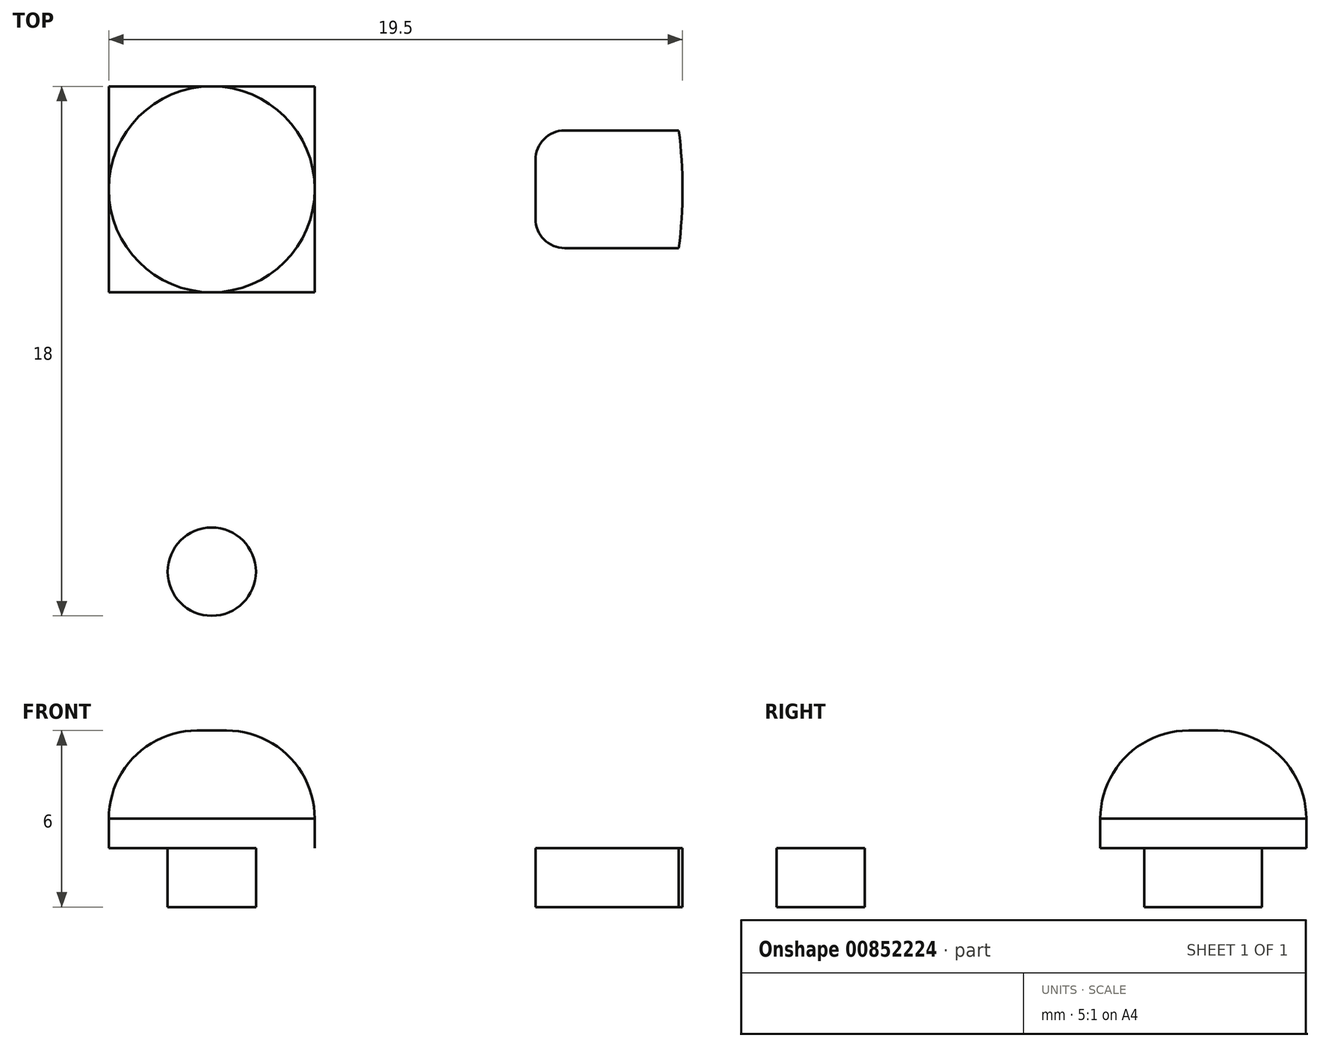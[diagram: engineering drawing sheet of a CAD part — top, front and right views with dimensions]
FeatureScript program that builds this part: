
annotation { "Feature Type Name" : "Feature", "Feature Type Description" : "" }
export const myFeature = defineFeature(function(context is Context, id is Id, definition is map)
    precondition{}
    {
        {
            var Q0;
            Q0=qCreatedBy(makeId("Top.planeOp"),FACE);
            var sketch = newSketch(context, id + "F0", { "sketchPlane" : qUnion([Q0])});
            skCircle(sketch, "E0", {"center": v(0, 0) * mm, "radius": 16 * mm});
            skSolve(sketch);
        }
        {
            var Q0;
            Q0=makeQuery(id+"F0.imprint","IMPRINT",FACE,{"disambiguationData":[TD([[makeQuery(id+"F0.imprint","IMPRINT",EDGE,{"derivedFrom":sQuery(id+"F0.wireOp",EDGE,"E0")}),1.0]])]});
            extrude(context, id + "F1", {"entities" : qUnion([Q0]), "depth" : 2 * mm, "offsetDistance" : 25 * mm});
        }
        {
            var Q0;
            Q0=makeQuery(id+"F1.opExtrude","CAP_FACE",FACE,{"disambiguationData":[OSD([sQuery(id+"F0.wireOp",EDGE,"E0")])],"isStart":false});
            var sketch = newSketch(context, id + "F2", { "sketchPlane" : qUnion([Q0])});
            skLineSegment(sketch, "E1", {"start": v(20.93, 0) * mm, "end": v(-31.8, 0) * mm, "construction": true});
            skLineSegment(sketch, "E2.bottom", {"start": v(-12, 2) * mm, "end": v(-21, 2) * mm});
            skLineSegment(sketch, "E2.top", {"start": v(-12, -2) * mm, "end": v(-21, -2) * mm});
            skLineSegment(sketch, "E2.left", {"start": v(-11, 1) * mm, "end": v(-11, -1) * mm});
            skLineSegment(sketch, "E2.right", {"start": v(-21, 2) * mm, "end": v(-21, -2) * mm});
            skPoint(sketch, "E2.middle", {"position": v(-16, 0) * mm});
            skPoint(sketch, "E3.visualSharp", {"position": v(-11, 2) * mm});
            skArc(sketch, "E3.filletArc", {"start": v(-11, 1) * mm, "mid": v(-11.3, 1.7) * mm, "end": v(-12, 2) * mm});
            skPoint(sketch, "E4.visualSharp", {"position": v(-11, -2) * mm});
            skArc(sketch, "E4.filletArc", {"start": v(-12, -2) * mm, "mid": v(-11.3, -1.7) * mm, "end": v(-11, -1) * mm});
            skLineSegment(sketch, "E5", {"start": v(0, 25.34) * mm, "end": v(0, -23.5) * mm, "construction": true});
            skLineSegment(sketch, "E6.MirrorCS", {"start": v(12, 2) * mm, "end": v(21, 2) * mm});
            skLineSegment(sketch, "E7.MirrorCS", {"start": v(12, -2) * mm, "end": v(21, -2) * mm});
            skPoint(sketch, "E8.MirrorP", {"position": v(11, 2) * mm});
            skPoint(sketch, "E9.MirrorP", {"position": v(11, -2) * mm});
            skLineSegment(sketch, "E10.MirrorCS", {"start": v(21, 2) * mm, "end": v(21, -2) * mm});
            skArc(sketch, "E11.MirrorCS", {"start": v(11, 1) * mm, "mid": v(11.3, 1.7) * mm, "end": v(12, 2) * mm});
            skLineSegment(sketch, "E12.MirrorCS", {"start": v(11, 1) * mm, "end": v(11, -1) * mm});
            skArc(sketch, "E13.MirrorCS", {"start": v(12, -2) * mm, "mid": v(11.3, -1.7) * mm, "end": v(11, -1) * mm});
            skCircle(sketch, "E14", {"center": v(0, 13) * mm, "radius": 1.5 * mm});
            skCircle(sketch, "E15.MirrorC", {"center": v(0, -13) * mm, "radius": 1.5 * mm});
            skSolve(sketch);
        }
        {
            var Q0;
            Q0=makeQuery(id+"F2.imprint","IMPRINT",FACE,{"disambiguationData":[TD([[makeQuery(id+"F2.imprint","IMPRINT",EDGE,{"derivedFrom":sQuery(id+"F2.wireOp",EDGE,"E2.left")}),-1.0]])]});
            var Q1;
            {var subQ0=sQuery(id+"F2.wireOp",EDGE,"E2.right");Q1=makeQuery(id+"F2.imprint","IMPRINT",FACE,{"disambiguationData":[TD([[makeQuery(id+"F2.imprint","IMPRINT",EDGE,{"derivedFrom":subQ0}),1.0]])]});}
            var Q2;
            {var subQ4=sQuery(id+"F2.wireOp",EDGE,"E11.MirrorCS");Q2=makeQuery(id+"F2.imprint","IMPRINT",FACE,{"disambiguationData":[TD([[makeQuery(id+"F2.imprint","IMPRINT",EDGE,{"derivedFrom":subQ4}),-1.0]])]});}
            var Q3;
            {var subQ0=sQuery(id+"F2.wireOp",EDGE,"E10.MirrorCS");Q3=makeQuery(id+"F2.imprint","IMPRINT",FACE,{"disambiguationData":[TD([[makeQuery(id+"F2.imprint","IMPRINT",EDGE,{"derivedFrom":subQ0}),-1.0]])]});}
            var Q4;
            Q4=makeQuery(id+"F2.imprint","IMPRINT",FACE,{"disambiguationData":[TD([[makeQuery(id+"F2.imprint","IMPRINT",EDGE,{"derivedFrom":sQuery(id+"F2.wireOp",EDGE,"E14")}),1.0]])]});
            var Q5;
            Q5=makeQuery(id+"F2.imprint","IMPRINT",FACE,{"disambiguationData":[TD([[makeQuery(id+"F2.imprint","IMPRINT",EDGE,{"derivedFrom":sQuery(id+"F2.wireOp",EDGE,"E15.MirrorC")}),-1.0]])]});
            extrude(context, id + "F3", {"entities" : qUnion([Q0, Q1, Q2, Q3, Q4, Q5]), "operationType" : NewBodyOperationType.REMOVE, "endBound" : BoundingType.THROUGH_ALL, "oppositeDirection" : true, "depth" : 25 * mm, "offsetDistance" : 25 * mm});
        }
        {
            var Q0;
            Q0=makeQuery(id+"F1.opExtrude","CAP_FACE",FACE,{"disambiguationData":[OSD([sQuery(id+"F0.wireOp",EDGE,"E0")])],"isStart":false});
            var sketch = newSketch(context, id + "F4", { "sketchPlane" : qUnion([Q0])});
            skLineSegment(sketch, "E16.bottom", {"start": v(3.5, 3.5) * mm, "end": v(-3.5, 3.5) * mm});
            skLineSegment(sketch, "E16.top", {"start": v(3.5, -3.5) * mm, "end": v(-3.5, -3.5) * mm});
            skLineSegment(sketch, "E16.left", {"start": v(3.5, 3.5) * mm, "end": v(3.5, -3.5) * mm});
            skLineSegment(sketch, "E16.right", {"start": v(-3.5, 3.5) * mm, "end": v(-3.5, -3.5) * mm});
            skPoint(sketch, "E16.middle", {"position": v(0, 0) * mm});
            skSolve(sketch);
        }
        {
            var Q0;
            Q0=makeQuery(id+"F4.imprint","IMPRINT",FACE,{"disambiguationData":[TD([[makeQuery(id+"F4.imprint","IMPRINT",EDGE,{"derivedFrom":sQuery(id+"F4.wireOp",EDGE,"E16.bottom")}),1.0]])]});
            extrude(context, id + "F5", {"entities" : qUnion([Q0]), "depth" : 1 * mm, "offsetDistance" : 25 * mm});
        }
        {
            var Q0;
            Q0=makeQuery(id+"F5.opExtrude","CAP_FACE",FACE,{"disambiguationData":[OSD([sQuery(id+"F4.wireOp",EDGE,"E16.bottom"),sQuery(id+"F4.wireOp",EDGE,"E16.top"),sQuery(id+"F4.wireOp",EDGE,"E16.left"),sQuery(id+"F4.wireOp",EDGE,"E16.right")])],"isStart":false});
            var sketch = newSketch(context, id + "F6", { "sketchPlane" : qUnion([Q0])});
            skCircle(sketch, "E17", {"center": v(0, 0) * mm, "radius": 3.5 * mm});
            skSolve(sketch);
        }
        {
            var Q0;
            {var subQ0=sQuery(id+"F6.wireOp",EDGE,"E17");var subQ1=makeQuery(id+"F6.imprint","INTERSECT",VERTEX,{"derivedFrom":[makeQuery(id+"F5.opExtrude","CAP_EDGE",EDGE,{"disambiguationData":[OSD([sQuery(id+"F4.wireOp",EDGE,"E16.bottom")])],"isStart":false}),subQ0]});Q0=makeQuery(id+"F6.imprint","IMPRINT",FACE,{"disambiguationData":[TD([[makeQuery(id+"F6.imprint","IMPRINT",EDGE,{"disambiguationData":[TD([[subQ1,1.0]])],"derivedFrom":subQ0}),1.0]])]});}
            extrude(context, id + "F7", {"entities" : qUnion([Q0]), "depth" : 3 * mm, "offsetDistance" : 25 * mm});
        }
        {
            var Q0;
            Q0=makeQuery(id+"F7.opExtrude","CAP_EDGE",EDGE,{"disambiguationData":[OSD([sQuery(id+"F6.wireOp",EDGE,"E17")])],"isStart":false});
            fillet(context, id + "F8", {"entities" : qUnion([Q0]), "radius" : 3 * mm, "tangentPropagation" : true, "allowEdgeOverflow" : false});
        }
    });
